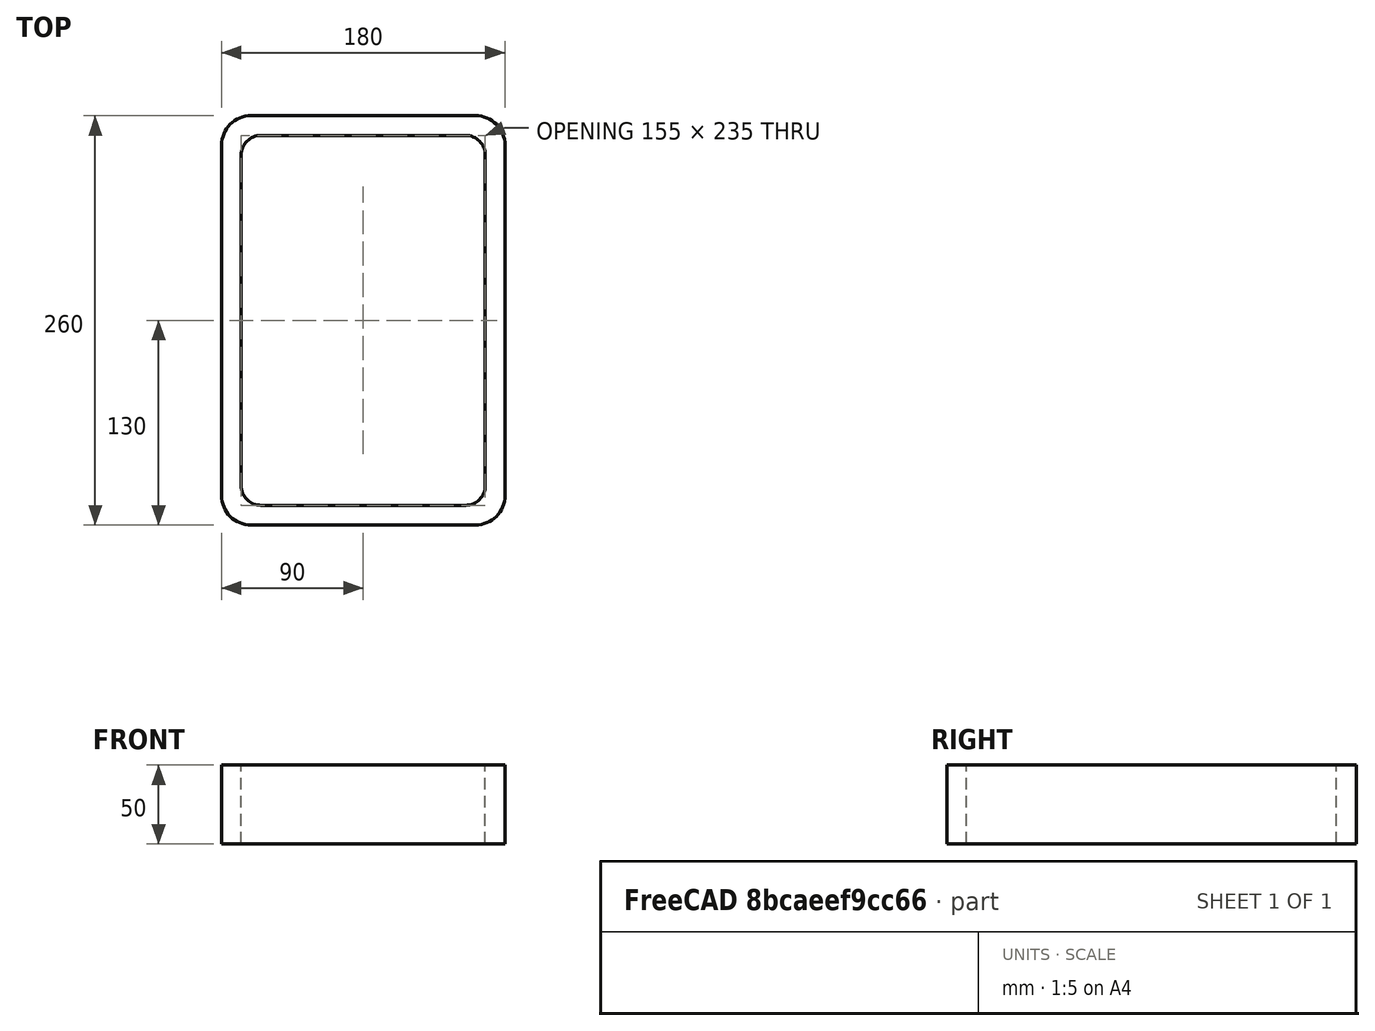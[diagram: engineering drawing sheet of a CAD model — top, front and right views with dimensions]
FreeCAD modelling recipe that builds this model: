
FCSTD DOCUMENT  (FreeCAD 0.15R4671 (Git))
Label: Rectangular hollow section 260x180x12.5 EN10219 S235JRH
License: All rights reserved
LicenseURL: http://en.wikipedia.org/wiki/All_rights_reserved
objects: Sketcher::SketchObject×1, Part::Extrusion×1
note: 2 computed .brp shape members not serialized (recipe doc carries the construction recipe); baked Part::Feature solids carry a one-line shape summary decoded from their .brp

FEATURE [Sketcher::SketchObject] Sketch
  sketch-geometry (16):
    g0: LineSegment StartX=-65 StartY=117.5 StartZ=0 EndX=65 EndY=117.5 EndZ=0
    g1: LineSegment StartX=77.5 StartY=105 StartZ=0 EndX=77.5 EndY=-105 EndZ=0
    g2: LineSegment StartX=65 StartY=-117.5 StartZ=0 EndX=-65 EndY=-117.5 EndZ=0
    g3: LineSegment StartX=-77.5 StartY=-105 StartZ=0 EndX=-77.5 EndY=105 EndZ=0
    g4: LineSegment StartX=-71.25 StartY=130 StartZ=0 EndX=71.25 EndY=130 EndZ=0
    g5: LineSegment StartX=90 StartY=111.25 StartZ=0 EndX=90 EndY=-111.25 EndZ=0
    g6: LineSegment StartX=71.25 StartY=-130 StartZ=0 EndX=-71.25 EndY=-130 EndZ=0
    g7: LineSegment StartX=-90 StartY=-111.25 StartZ=0 EndX=-90 EndY=111.25 EndZ=0
    g8: ArcOfCircle CenterX=-65 CenterY=105 CenterZ=0 NormalX=0 NormalY=0 NormalZ=1 Radius=12.5 StartAngle=1.5708 EndAngle=3.14159
    g9: ArcOfCircle CenterX=65 CenterY=105 CenterZ=0 NormalX=0 NormalY=0 NormalZ=1 Radius=12.5 StartAngle=0 EndAngle=1.5708
    g10: ArcOfCircle CenterX=65 CenterY=-105 CenterZ=0 NormalX=0 NormalY=0 NormalZ=1 Radius=12.5 StartAngle=4.71239 EndAngle=6.28319
    g11: ArcOfCircle CenterX=-65 CenterY=-105 CenterZ=0 NormalX=0 NormalY=0 NormalZ=1 Radius=12.5 StartAngle=3.14159 EndAngle=4.71239
    g12: ArcOfCircle CenterX=71.25 CenterY=111.25 CenterZ=0 NormalX=0 NormalY=0 NormalZ=1 Radius=18.75 StartAngle=0 EndAngle=1.5708
    g13: ArcOfCircle CenterX=71.25 CenterY=-111.25 CenterZ=0 NormalX=0 NormalY=0 NormalZ=1 Radius=18.75 StartAngle=4.71239 EndAngle=6.28319
    g14: ArcOfCircle CenterX=-71.25 CenterY=-111.25 CenterZ=0 NormalX=0 NormalY=0 NormalZ=1 Radius=18.75 StartAngle=3.14159 EndAngle=4.71239
    g15: ArcOfCircle CenterX=-71.25 CenterY=111.25 CenterZ=0 NormalX=0 NormalY=0 NormalZ=1 Radius=18.75 StartAngle=1.5708 EndAngle=3.14159
  constraints (36):
    c: Horizontal(g2)
    c: Vertical(g3)
    c: Horizontal(g6)
    c: Vertical(g7)
    c: Tangent(g3,g8) = 1.5708
    c: Tangent(g0,g8) = 1.5708
    c: Tangent(g0,g9) = 1.5708
    c: Tangent(g1,g9) = 1.5708
    c: Tangent(g1,g10) = 1.5708
    c: Tangent(g2,g10) = 1.5708
    c: Tangent(g2,g11) = 1.5708
    c: Tangent(g3,g11) = 1.5708
    c: Tangent(g4,g12) = 1.5708
    c: Tangent(g5,g12) = 1.5708
    c: Tangent(g5,g13) = 1.5708
    c: Tangent(g6,g13) = 1.5708
    c: Tangent(g6,g14) = 1.5708
    c: Tangent(g7,g14) = 1.5708
    c: Tangent(g7,g15) = 1.5708
    c: Tangent(g4,g15) = 1.5708
    c: Equal(g9,g8)
    c: Equal(g9,g11)
    c: Equal(g9,g10)
    c: Equal(g12,g15)
    c: Equal(g12,g14)
    c: Equal(g12,g13)
    c: Symmetric(g4,g6,g-1)
    c: Symmetric(g7,g5,g-2)
    c: DistanceY(g4,g6) = -260
    c: DistanceX(g7,g5) = 180
    c: Symmetric(g3,g1,g-2)
    c: Symmetric(g0,g2,g-1)
    c: DistanceY(g0,g4) = 12.5
    c: DistanceX(g5,g1) = -12.5
    c: Radius(g9) = 12.5
    c: Radius(g12) = 18.75
FEATURE [Part::Extrusion] Extrude  label="Rectangular hollow section 260x180x12.5 EN10219 S235JRH"
  Base = -> Sketch
  Dir = (0,0,50)
  Solid = true
